# Revit family: DC_Rheem_PLM_Raypak_B0768HWT
name_source: partatom
category: Plumbing Fixtures
units: mm (PartAtom-declared; Revit-internal decimal feet)

## family parameters
Cut with Voids When Loaded = No
Host = Face
Part Type = Normal
Room Calculation Point = No
Round Connector Dimension = Use Radius
Shared = No

## types (4) — shared parameters
Basae2Dist_ANZRS = 95 mm  [stored 0.31168 ft]
Base1Dist_ANZRS = 75 mm
BaseHeight_ANZRS = 35 mm
BaseWidth_ANZRS = 55 mm
BoxHeight_ANZRS = 975 mm
ColdWaterConn.Dist_ANZRS = 280 mm  [stored 0.918635 ft]
ColdWaterInletDiameter_ANZRS = 65 mm
ColdWaterInletRadius_ANZRS = 33 mm
ConnHeight_ANZRS = 745 mm
EleBoxHeightFromBase_ANZRS = 235 mm  [stored 0.770997 ft]
EleBoxHeight_ANZRS = 380 mm  [stored 1.24672 ft]
EleBoxW_ANZRS = 160 mm
GasConn.Dist_ANZRS = 95 mm  [stored 0.31168 ft]
GasInletHeight_ANZRS = 435 mm
H1_ANZRS = 935 mm
Height_ANZRS = 2255 mm
HotWaterConn.Dist_ANZRS = 155 mm  [stored 0.50853 ft]
HotWateroutletDiameter_ANZRS = 65 mm
HotWateroutletradius_ANZRS = 33 mm
L1_ANZRS = 387 mm
Length_ANZRS = 750 mm  [stored 2.46063 ft]
Manufacturer = Raypak
Materials_ANZRS = Raypak - Grey Powder Coated Steel
PRV_ANZRS = 15 mm  [stored 0.0492126 ft]
PVRDist_ANZRS = 85 mm  [stored 0.278871 ft]
T_ANZRS = 50 mm  [stored 0.164042 ft]
TopDiaBig_ANZRS = 450 mm
TopDiaSmall_ANZRS = 225 mm
TopH1_ANZRS = 150 mm
TopH2_ANZRS = 275 mm
URL = http://www.rheem.com.au
Width_ANZRS = 1055 mm  [stored 3.46129 ft]
zero-valued in all types: Default Elevation

## per-type parameters (varying)
| type | GasInletDiameter_ANZRS | GasInletradius_ANZRS | Model | Type Comments |
| Raypak - Gas Water Heater- Outdoor - 765 MJ/h  Natural gas, modulating gas control | 40 mm | 20 mm  [stored 0.0656168 ft] | B0768NCM/HWT | Recovery 2924L/h @ 50°C rise |
| Raypak - Gas Water Heater- Outdoor - 765 MJ/h  Natural gas, On/Off gas control | 40 mm | 20 mm  [stored 0.0656168 ft] | B0768NCO/HWT | Recovery 2924L/h @ 50°C rise |
| Raypak - Gas Water Heater- Outdoor - 720 MJ/h  Propane gas, modulating gas control | 20 mm  [stored 0.0656168 ft] | 10 mm  [stored 0.0328084 ft] | B0768PCM/HWT | Recovery 2752L/h @ 50°C rise |
| Raypak - Gas Water Heater- Outdoor - 720 MJ/h  Propane gas, On/Off gas control | 32 mm | 16 mm  [stored 0.0524934 ft] | B0768PCO/HWT | Recovery 2752L/h @ 50°C rise |

note: column(s) folded — value = type name in every type: Description

note: [stored X ft] marks values corroborated as IEEE doubles in the binary element streams (Revit-internal decimal feet)

## geometry (parser evidence)
native form markers: Blend x6, Sweep x2
no freeform markers — native parametric forms only
